# Revit family: GC-100
name_source: partatom
category: Mechanical Equipment
units: mm (PartAtom-declared; Revit-internal decimal feet)

## family parameters
Always vertical = Yes
Cut with Voids When Loaded = No
Part Type = Normal
Room Calculation Point = No
Round Connector Dimension = Use Radius
Shared = No
Work Plane-Based = No

## types (15) — shared parameters
Manufacturer = Loren Cook Company
ONE EIGTHT = 0' - 0 1/8"
T0 = 0' - 5 13/32"
T1 = 0' - 8 3/8"
T10 = 0' - 4"
T11 = 2' - 0"
T12 = 0' - 2"
T13 = 0' - 7 3/4"
T14 = 0' - 1"
T15 = 0' - 1 1/2"
T16 = 0' - 0 5/8"
T2 = 0' - 7"
T3 = 0' - 3 7/16"
T4 = 0' - 6 1/2"
T5 = 0' - 6"
T6 = 0' - 2 31/32"
T7 = 0' - 2 27/32"
T8 = 0' - 3 1/4"
T9 = 0' - 3"
Type Comments = Ceiling Fans 100 Series
URL = www.lorencook.com
Zero = 0' - 0"

## per-type parameters (varying)
| type | A | A/2 | B | B/2 | Model |
| GC-126/128_PLASTIC | 1' - 1 1/4" | 0' - 6 5/8" | 1' - 2 3/4" | 0' - 7 3/8" | GC |
| GC-146/148_PLASTIC | 1' - 1 1/4" | 0' - 6 5/8" | 1' - 2 3/4" | 0' - 7 3/8" | GC |
| GC-166/168_PLASTIC | 1' - 1 1/4" | 0' - 6 5/8" | 1' - 2 3/4" | 0' - 7 3/8" | GC |
| GC-186/188_PLASTIC | 1' - 1 1/4" | 0' - 6 5/8" | 1' - 2 3/4" | 0' - 7 3/8" | GC |
| GC-186/188_STEEL | 1' - 1 1/2" | 0' - 6 3/4" | 1' - 3 1/2" | 0' - 7 3/4" | GC |
| GC-166/168_STEEL | 1' - 1 1/2" | 0' - 6 3/4" | 1' - 3 1/2" | 0' - 7 3/4" | GC |
| GC-146/148_STEEL | 1' - 1 1/2" | 0' - 6 3/4" | 1' - 3 1/2" | 0' - 7 3/4" | GC |
| GC-126/128_STEEL | 1' - 1 1/2" | 0' - 6 3/4" | 1' - 3 1/2" | 0' - 7 3/4" | GC |
| GC-186/188_ALUMINUM | 1' - 0 3/4" | 0' - 6 3/8" | 1' - 2 3/4" | 0' - 7 3/8" | GC |
| GC-166/168_ALUMINUM | 1' - 0 3/4" | 0' - 6 3/8" | 1' - 2 3/4" | 0' - 7 3/8" | GC |
| GC-146/148_ALUMINUM | 1' - 0 3/4" | 0' - 6 3/8" | 1' - 2 3/4" | 0' - 7 3/8" | GC |
| GC-126/128_ALUMINUM | 1' - 0 3/4" | 0' - 6 3/8" | 1' - 2 3/4" | 0' - 7 3/8" | GC |
| GCVF-100_ALUMINUM | 1' - 0 3/4" | 0' - 6 3/8" | 1' - 2 3/4" | 0' - 7 3/8" | GCVF |
| GCVF-100_PLATSTIC | 1' - 1 1/4" | 0' - 6 5/8" | 1' - 2 3/4" | 0' - 7 3/8" | GCVF |
| GCVF-100_STEEL | 1' - 1 1/2" | 0' - 6 3/4" | 1' - 3 1/2" | 0' - 7 3/4" | GCVF |

## geometry (parser evidence)
native form markers: Sweep x2
no freeform markers — native parametric forms only
